# Revit family: 58149103(2021)
name_source: partatom
category: Plumbing Fixtures
revit_build: Autodesk Revit 2018 (Build: 20190510_1515(x64)
units: mm (PartAtom-declared; Revit-internal decimal feet)

## family parameters
Always vertical = Yes
Cut with Voids When Loaded = No
OmniClass Number = 23.45.55.00
OmniClass Title = Sanitary Faucets, Wastes
Part Type = Normal
Room Calculation Point = No
Round Connector Dimension = Use Diameter
Shared = No
Work Plane-Based = No

## types (1)
- 58149103 Shower system
    2D/3D/BIM Files URL = http://static.hansa.com
    Advanced Features = DZR brass
    AssetType = Fixed
    BIMObjectName = 58149103(2021)
    Backflow Prevention EN1717 = EB
    BodyMaterial = Brass
    Brand = Hansa
    Catalog Drawing URL = http://static.hansa.com
    Category = Bathroom;Shower
    Class = Thermostatic
    CloseOffRating = 0
    Color = Chrome
    Connection = Eccentric unions;;
    Customs Code = 84818011
    DN Size = DN15
    Dimension Drawing URL = http://static.hansa.com
    DurationUnit = Year
    EAN Number = 4015474253353
    EN Standard = EN 1111, EN 1112, EN 1113
    FDV Document URL = http://www.hansa.com
    FaucetMainMaterial = Brass
    FaucetNominalDepth = 606 mm
    FaucetNominalHeight = 1162 mm
    FaucetNominalWidth = 296 mm
    Features = Thermostatic
    Finish = Polished
    Flow Drawing URL = http://static.hansa.com
    Flow Rate At 300kPa = 200.2 L/s
    FlowCoefficient = 0
    Group = Shower systems
    Hand Shower Size = Ø 100 mm
    IfcExportAs = IfcValveType
    IfcExportType = FAUCET
    Installation Type = Wall mounted
    Installation Width = cc150 ± 15 mm
    Installation and Maintenance = http://static.hansa.com
    LVI Number = 6310767
    Lever Handle = Temperature control handle;Flow control handle
    Manufacturer = Hansa
    ManufacturerName = Hansa
    ManufacturerURL = http://www.hansa.com
    Market = AUT;BEL;CZE;DEU;ESP;FRA;INT;ITA;NLD;SVK
    Material = Brass
    Max. Hot Water Supply = 65 °C
    Mechanical Parts = Ceramic head part;Non-return valve(s);Litter filter(s)
    Model = 58149103 Shower system
    ModelReference = 58149103
    NBSDescription = Water supply fittings for baths
    NBSReference = 45-35-70/315
    NRF Number = 4202528
    Name = 58149103 Shower system
    Name_en = 58149103 Shower system
    Noise Class = I (ISO 3822)
    Over Head Shower Size = Ø 202 mm
    Package Weight = 6.48 kg
    Package external Dimensions = 838 x 318 x 97
    Pressure Loss With Flow 02ls = 300000.0 Pa
    Product Code = 58149103
    Product Datasheet = http://www.hansa.com
    Product Family = HANSAUNITA
    Product Image URL = http://static.hansa.com
    Product URL = http://static.hansa.com
    Projection = 481 mm
    RSK Number = 8343765
    Shape = Sculptured
    Shower Parts = Hand shower;Shower rail;Shower head;Shower bracket adjustable;Shower Hose (1250 mm)
    Shower Spray = Classic;Intense;Rain
    Shower Spray Number = 3spray
    Size = 295x605x1165 mm
    Spare Parts = http://static.hansa.com
    Technical DataSheet URL = http://www.hansa.com
    Temperature = Thermostatic temperature control
    Temperature Adjustments = Thermostatic safety stop at 38°C;THERMO COOL
    Uniclass2 = Pr_40_30_96_78
    Uniclass2015Description = Shower manual water supply sets
    Uniclass2015Reference = Pr_40_20_87_78
    VVS Number = 722979804
    Version = 1
    VersionDate = 08/03/2021
    WarrantyDescription = http://warranty.hansa.com
    WarrantyDurationUnit = Year
    WorkingPressure = 100 - 1000 kPa

## geometry (parser evidence)
native form markers: Sweep x5
no freeform markers — native parametric forms only
